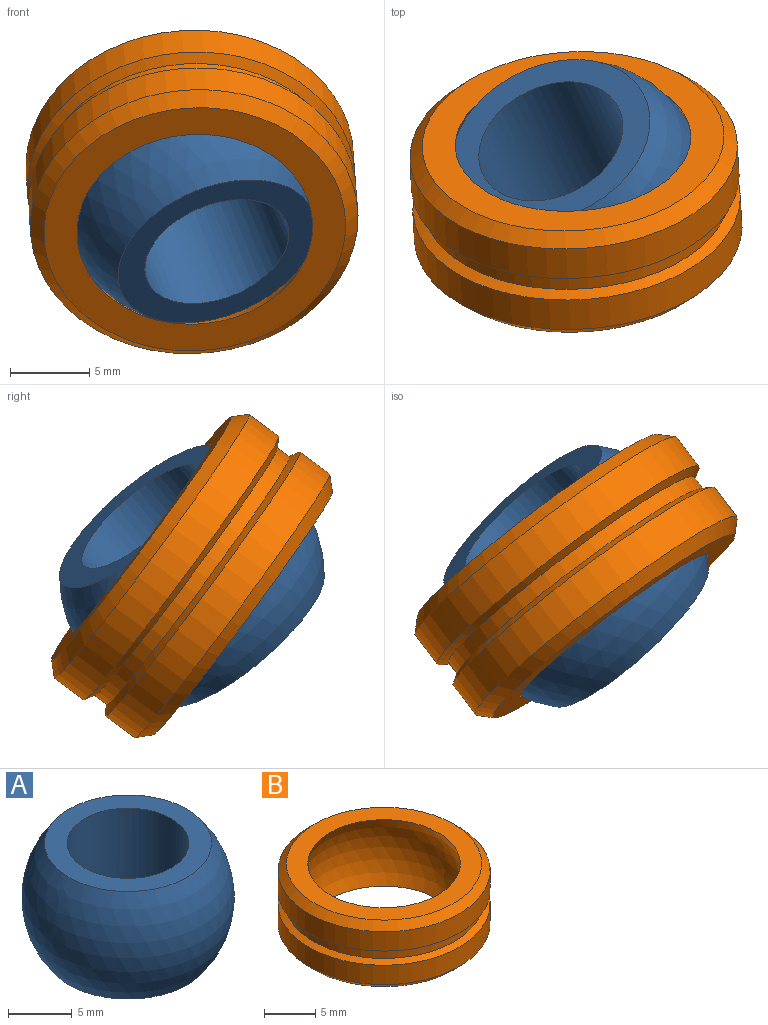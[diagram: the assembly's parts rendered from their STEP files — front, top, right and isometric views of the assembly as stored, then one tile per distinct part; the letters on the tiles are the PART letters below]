
ASSEMBLY  parts=2 mates=1
PART A: 4 faces, bbox 16.7x16.7x10.3 mm
  f0: cylinder r=4.76mm len=10.31mm, axis (0,0,1), area 308.6mm2, adj f2,f3
  f1: sphere r=8.33mm, area 539.8mm2, adj f2,f3
  f2: plane 13.09x13.09mm, normal (0,0,1), area 63.3mm2, adj f0,f1
  f3: plane 13.09x13.09mm, normal (0,0,-1), area 63.3mm2, adj f0,f1
PART B: 10 faces, bbox 20.6x20.6x7.9 mm
  f0: cone r=9.68mm half-angle=60deg, axis (0,0,-1), area 46.1mm2, adj f1,f6
  f1: cylinder r=9.68mm len=19.37mm, axis (0,0,1), area 57.9mm2, adj f0,f2
  f2: cone r=10.32mm half-angle=60deg, axis (0,0,1), area 46.1mm2, adj f1,f7
  f3: cone r=10.32mm half-angle=45deg, axis (0,0,1), area 71.6mm2, adj f6,f9
  f4: cone r=9.51mm half-angle=45deg, axis (0,0,-1), area 71.6mm2, adj f7,f8
  f5: sphere r=8.41mm, area 419mm2, adj f8,f9
  f6: cylinder r=10.32mm len=20.64mm, axis (0,0,-1), area 149.6mm2, adj f0,f3
  f7: cylinder r=10.32mm len=20.64mm, axis (0,0,-1), area 149.6mm2, adj f2,f4
  f8: plane 19.01x19.01mm, normal (0,0,1), area 110.8mm2, adj f4,f5
  f9: plane 19.01x19.01mm, normal (0,0,-1), area 110.8mm2, adj f3,f5
PLACE A rot(axis=(-0.82,-0.52,-0.24),44.8deg) t=(-1.77,2.81,1.03)mm
PLACE B rot(axis=(0.89,-0.4,0.23),132.9deg) t=(-1.77,2.81,1.03)mm
MATE ball A.f0 <-> B.f0  axis (-0.31,0.62,0.73) through (-1.77,2.81,1.03)mm
